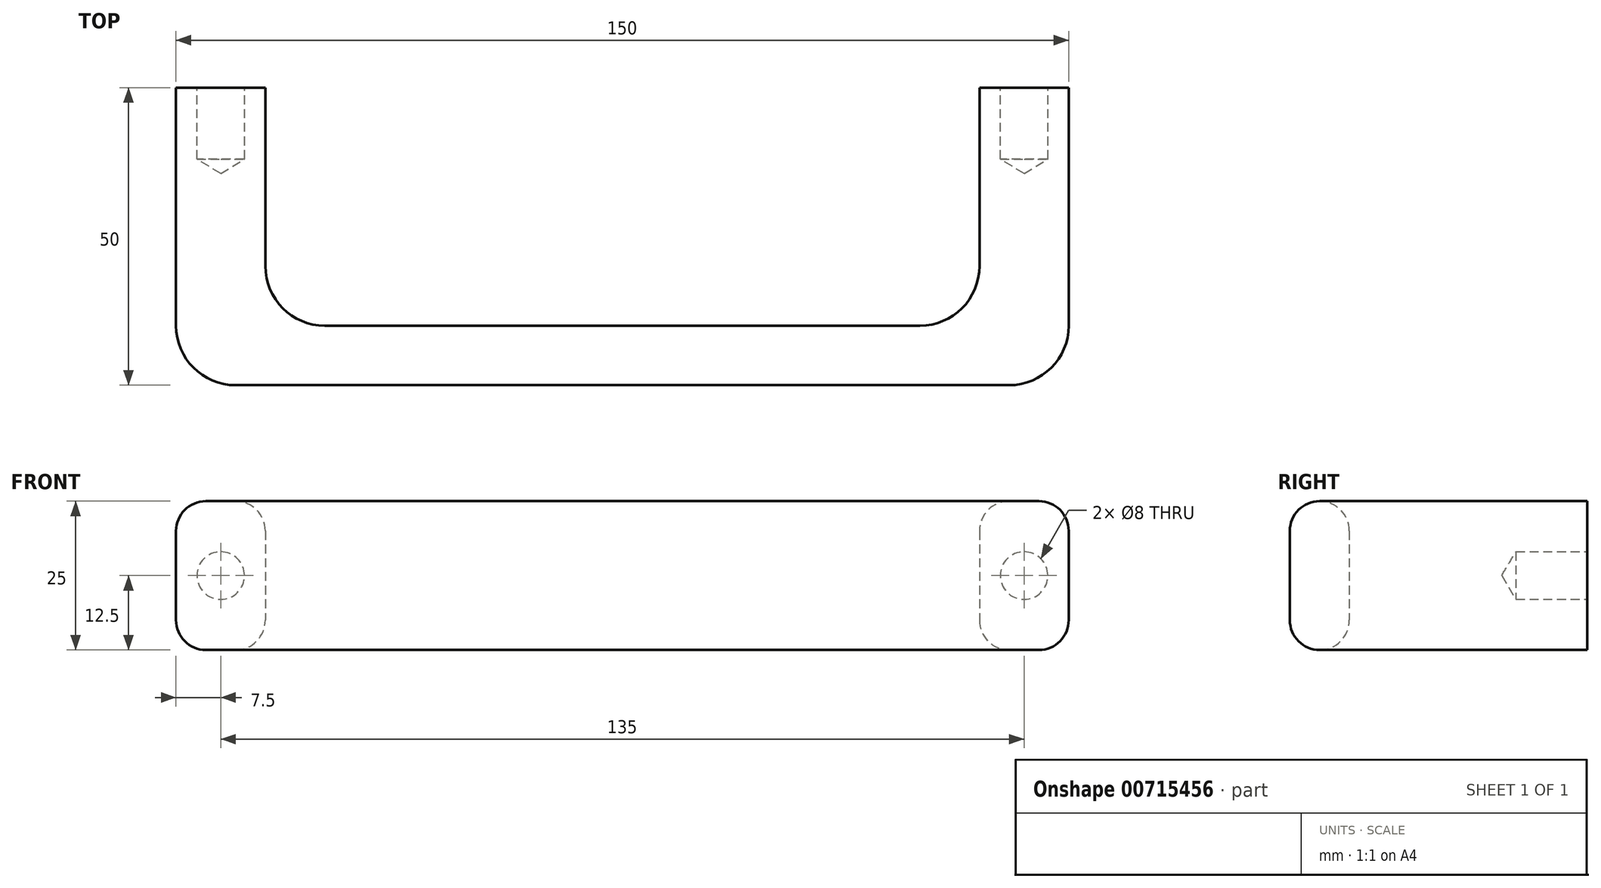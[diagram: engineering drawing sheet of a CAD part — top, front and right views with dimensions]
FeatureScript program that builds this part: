
annotation { "Feature Type Name" : "Feature", "Feature Type Description" : "" }
export const myFeature = defineFeature(function(context is Context, id is Id, definition is map)
    precondition{}
    {
        {
            var Q0;
            Q0=qCreatedBy(makeId("Top.planeOp"),FACE);
            var sketch = newSketch(context, id + "F0", { "sketchPlane" : qUnion([Q0])});
            skLineSegment(sketch, "E0.bottom", {"start": v(75, 25) * mm, "end": v(60, 25) * mm});
            skLineSegment(sketch, "E0.top", {"start": v(65, -25) * mm, "end": v(-65, -25) * mm});
            skLineSegment(sketch, "E0.left", {"start": v(75, 25) * mm, "end": v(75, -15) * mm});
            skLineSegment(sketch, "E0.right", {"start": v(-75, 25) * mm, "end": v(-75, -15) * mm});
            skPoint(sketch, "E0.middle", {"position": v(0, 0) * mm});
            skLineSegment(sketch, "E1.top", {"start": v(-50, -15) * mm, "end": v(50, -15) * mm});
            skLineSegment(sketch, "E1.left", {"start": v(-60, 25) * mm, "end": v(-60, -5) * mm});
            skLineSegment(sketch, "E1.right", {"start": v(60, 25) * mm, "end": v(60, -5) * mm});
            skLineSegment(sketch, "E2.trimOffspring", {"start": v(-60, 25) * mm, "end": v(-75, 25) * mm});
            skPoint(sketch, "E3.visualSharp", {"position": v(60, -15) * mm});
            skArc(sketch, "E3.filletArc", {"start": v(50, -15) * mm, "mid": v(57.07, -12.07) * mm, "end": v(60, -5) * mm});
            skPoint(sketch, "E4.visualSharp", {"position": v(75, -25) * mm});
            skArc(sketch, "E4.filletArc", {"start": v(65, -25) * mm, "mid": v(72.07, -22.07) * mm, "end": v(75, -15) * mm});
            skPoint(sketch, "E5.visualSharp", {"position": v(-60, -15) * mm});
            skArc(sketch, "E5.filletArc", {"start": v(-60, -5) * mm, "mid": v(-57.07, -12.07) * mm, "end": v(-50, -15) * mm});
            skPoint(sketch, "E6.visualSharp", {"position": v(-75, -25) * mm});
            skArc(sketch, "E6.filletArc", {"start": v(-75, -15) * mm, "mid": v(-72.07, -22.07) * mm, "end": v(-65, -25) * mm});
            skSolve(sketch);
        }
        {
            var Q0;
            Q0=makeQuery(id+"F0.imprint","IMPRINT",FACE,{"disambiguationData":[TD([[makeQuery(id+"F0.imprint","IMPRINT",EDGE,{"derivedFrom":sQuery(id+"F0.wireOp",EDGE,"E0.bottom")}),1.0]])]});
            extrude(context, id + "F1", {"entities" : qUnion([Q0]), "depth" : 25 * mm, "offsetDistance" : 25 * mm});
        }
        {
            var Q0;
            Q0=makeQuery(id+"F1.opExtrude","CAP_EDGE",EDGE,{"disambiguationData":[OSD([sQuery(id+"F0.wireOp",EDGE,"E5.filletArc")])],"isStart":true});
            var Q1;
            Q1=makeQuery(id+"F1.opExtrude","CAP_EDGE",EDGE,{"disambiguationData":[OSD([sQuery(id+"F0.wireOp",EDGE,"E5.filletArc")])],"isStart":false});
            var Q2;
            Q2=makeQuery(id+"F1.opExtrude","CAP_EDGE",EDGE,{"disambiguationData":[OSD([sQuery(id+"F0.wireOp",EDGE,"E6.filletArc")])],"isStart":true});
            var Q3;
            Q3=makeQuery(id+"F1.opExtrude","CAP_EDGE",EDGE,{"disambiguationData":[OSD([sQuery(id+"F0.wireOp",EDGE,"E6.filletArc")])],"isStart":false});
            fillet(context, id + "F2", {"entities" : qUnion([Q0, Q1, Q2, Q3]), "radius" : 5 * mm, "tangentPropagation" : true, "allowEdgeOverflow" : false});
        }
        {
            var Q0;
            Q0=makeQuery(id+"F1.opExtrude","SWEPT_FACE",FACE,{"disambiguationData":[OSD([sQuery(id+"F0.wireOp",EDGE,"E2.trimOffspring")])]});
            var sketch = newSketch(context, id + "F3", { "sketchPlane" : qUnion([Q0])});
            skCircle(sketch, "E7", {"center": v(67.5, 12.5) * mm, "radius": 3 * mm});
            skSolve(sketch);
        }
        {
            var Q0;
            Q0=sQuery(id+"F3.wireOp",VERTEX,"E7.center");
            var Q1;
            Q1=makeQuery(id+"F1.opExtrude","SWEPT_BODY",BODY,{"disambiguationData":[OSD([sQuery(id+"F0.wireOp",EDGE,"E0.bottom"),sQuery(id+"F0.wireOp",EDGE,"E0.top"),sQuery(id+"F0.wireOp",EDGE,"E0.left"),sQuery(id+"F0.wireOp",EDGE,"E0.right"),sQuery(id+"F0.wireOp",EDGE,"E1.top"),sQuery(id+"F0.wireOp",EDGE,"E1.left"),sQuery(id+"F0.wireOp",EDGE,"E1.right"),sQuery(id+"F0.wireOp",EDGE,"E2.trimOffspring"),sQuery(id+"F0.wireOp",EDGE,"E3.filletArc"),sQuery(id+"F0.wireOp",EDGE,"E4.filletArc"),sQuery(id+"F0.wireOp",EDGE,"E5.filletArc"),sQuery(id+"F0.wireOp",EDGE,"E6.filletArc")])]});
            hole(context, id + "F4", {"style" : HoleStyle.SIMPLE, "endStyle" : HoleEndStyle.BLIND, "holeDiameter" : 8 * mm, "majorDiameter" : 5 * mm, "holeDepth" : 12 * mm, "isTappedThrough" : true, "tappedDepth" : 12 * mm, "tapClearance" : 3, "locations" : qUnion([Q0]), "scope" : qUnion([Q1])});
        }
        {
            var Q0;
            Q0=makeQuery(id+"F1.opExtrude","SWEPT_FACE",FACE,{"disambiguationData":[OSD([sQuery(id+"F0.wireOp",EDGE,"E0.bottom")])]});
            var sketch = newSketch(context, id + "F5", { "sketchPlane" : qUnion([Q0])});
            skCircle(sketch, "E8", {"center": v(-67.5, 12.5) * mm, "radius": 4 * mm});
            skSolve(sketch);
        }
        {
            var Q0;
            Q0=sQuery(id+"F5.wireOp",VERTEX,"E8.center");
            var Q1;
            Q1=makeQuery(id+"F1.opExtrude","SWEPT_BODY",BODY,{"disambiguationData":[OSD([sQuery(id+"F0.wireOp",EDGE,"E0.bottom"),sQuery(id+"F0.wireOp",EDGE,"E0.top"),sQuery(id+"F0.wireOp",EDGE,"E0.left"),sQuery(id+"F0.wireOp",EDGE,"E0.right"),sQuery(id+"F0.wireOp",EDGE,"E1.top"),sQuery(id+"F0.wireOp",EDGE,"E1.left"),sQuery(id+"F0.wireOp",EDGE,"E1.right"),sQuery(id+"F0.wireOp",EDGE,"E2.trimOffspring"),sQuery(id+"F0.wireOp",EDGE,"E3.filletArc"),sQuery(id+"F0.wireOp",EDGE,"E4.filletArc"),sQuery(id+"F0.wireOp",EDGE,"E5.filletArc"),sQuery(id+"F0.wireOp",EDGE,"E6.filletArc")])]});
            hole(context, id + "F6", {"style" : HoleStyle.SIMPLE, "endStyle" : HoleEndStyle.BLIND, "holeDiameter" : 8 * mm, "majorDiameter" : 5 * mm, "holeDepth" : 12 * mm, "isTappedThrough" : true, "tappedDepth" : 12 * mm, "tapClearance" : 3, "locations" : qUnion([Q0]), "scope" : qUnion([Q1])});
        }
    });
